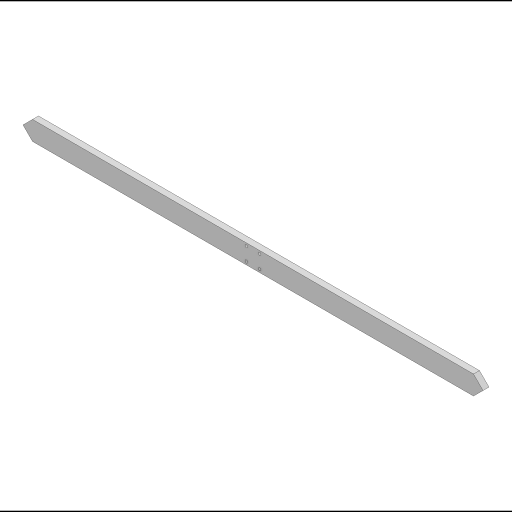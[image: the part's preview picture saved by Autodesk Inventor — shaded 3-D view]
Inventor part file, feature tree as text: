
AUTODESK INVENTOR PART (.ipt)
format: ipt  version: 2023 (Build 270158000, 158)  size: 105,472 bytes
history: native  units: in
note: dims shown in document units (in); Inventor stores cm internally (conversion verified against a paired STEP export)
features: extrude x2, sketch x2
ambient origin geometry x8: Origin, YZ Plane, XZ Plane, XY Plane, X Axis, Y Axis, Z Axis, Center Point
bodies: Solid1 (feature_tree)
feature tree (4):
  extrude  "Extrusion1"  TaperAngle=45.0deg  [1 undecoded]
  extrude  "Extrusion2"  Depth=1.0in
  sketch  "Sketch1"  dims[d0=90.0deg d1=45.0deg]
  sketch  "Sketch2"  dims[d2=24.127in d3=1.0in d4=0.5in d5=0.0in d6=0.3125in d7=0.0in d8=12.0635in d9=0.9843in d10=0.1378in d11=0.1378in d12=0.1378in d13=0.1378in d14=0.0in d15=0.0in]
note: 1 required parameter value undecoded (feature->parameter linkage not recoverable at this tier; creation-order binding heuristic only, values carry confidence <= 0.55)
